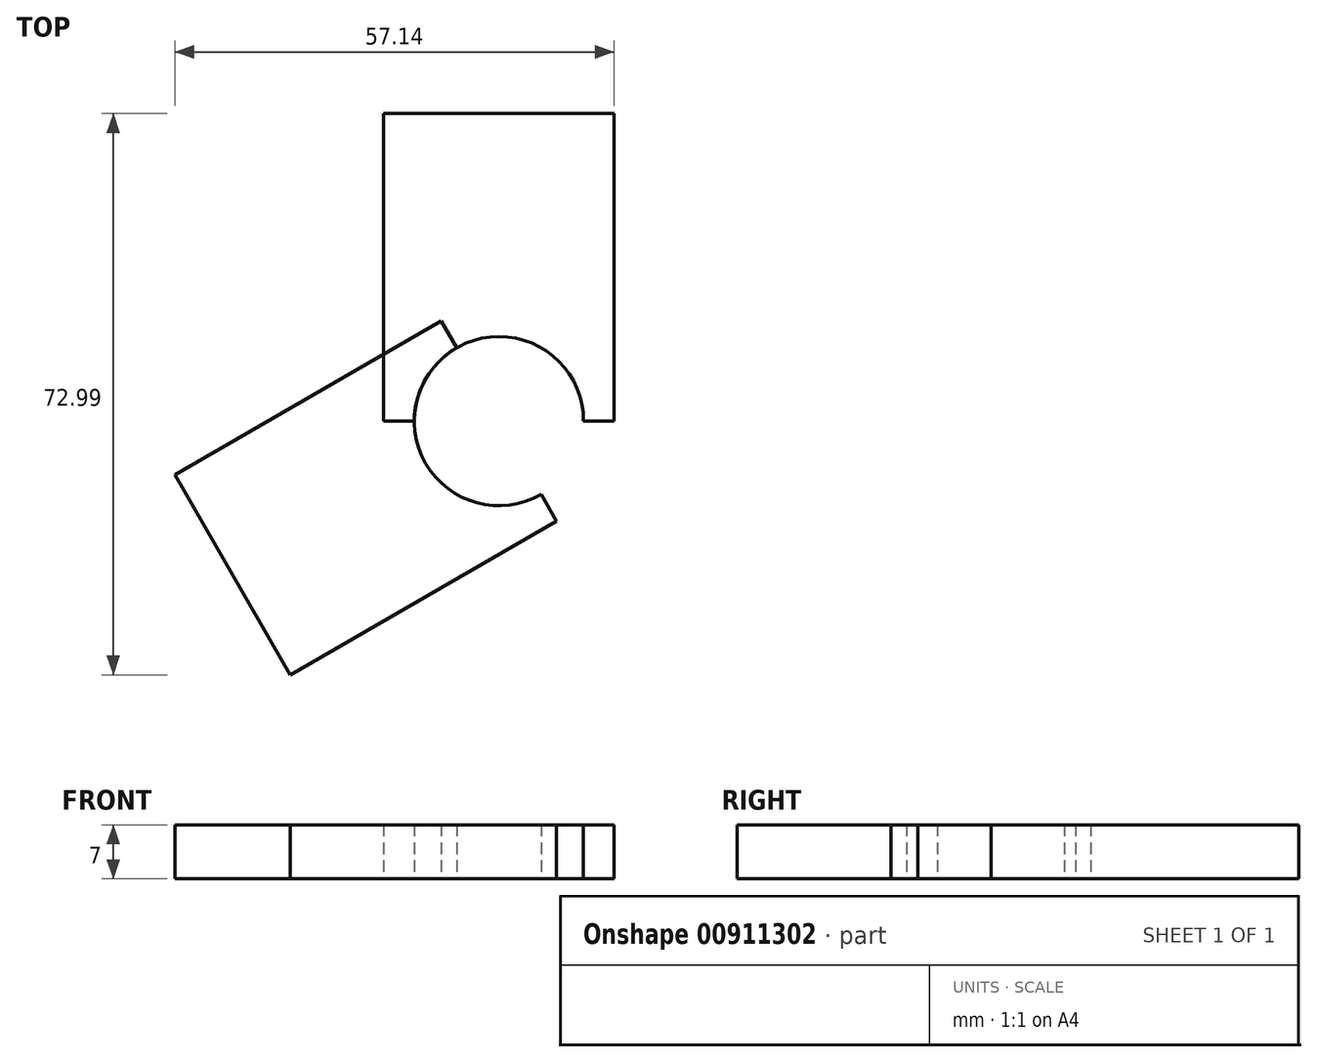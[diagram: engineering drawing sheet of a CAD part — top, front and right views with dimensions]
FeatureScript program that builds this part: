
annotation { "Feature Type Name" : "Feature", "Feature Type Description" : "" }
export const myFeature = defineFeature(function(context is Context, id is Id, definition is map)
    precondition{}
    {
        {
            var Q0;
            Q0=qCreatedBy(makeId("Top.planeOp"),FACE);
            var sketch = newSketch(context, id + "F0", { "sketchPlane" : qUnion([Q0])});
            skCircle(sketch, "E0", {"center": v(0, 0) * mm, "radius": 11 * mm});
            skLineSegment(sketch, "E1", {"start": v(0, 0) * mm, "end": v(0, 40) * mm});
            skLineSegment(sketch, "E2", {"start": v(0, 40) * mm, "end": v(15, 40) * mm});
            skLineSegment(sketch, "E3", {"start": v(15, 40) * mm, "end": v(15, 0) * mm});
            skLineSegment(sketch, "E4", {"start": v(15, 0) * mm, "end": v(0, 0) * mm});
            skLineSegment(sketch, "E5", {"start": v(0, 0) * mm, "end": v(-15, 0) * mm});
            skLineSegment(sketch, "E6", {"start": v(-15, 0) * mm, "end": v(-15, 40) * mm});
            skLineSegment(sketch, "E7", {"start": v(-15, 40) * mm, "end": v(0, 40) * mm});
            skSolve(sketch);
        }
        {
            var Q0;
            {var subQ0=sQuery(id+"F0.wireOp",EDGE,"E6");Q0=makeQuery(id+"F0.imprint","IMPRINT",FACE,{"disambiguationData":[TD([[makeQuery(id+"F0.imprint","IMPRINT",EDGE,{"derivedFrom":subQ0}),-1.0]])]});}
            var Q1;
            {var subQ1=sQuery(id+"F0.wireOp",EDGE,"E2");Q1=makeQuery(id+"F0.imprint","IMPRINT",FACE,{"disambiguationData":[TD([[makeQuery(id+"F0.imprint","IMPRINT",EDGE,{"derivedFrom":subQ1}),-1.0]])]});}
            extrude(context, id + "F1", {"entities" : qUnion([Q0, Q1]), "depth" : 7 * mm, "offsetDistance" : 25 * mm});
        }
        {
            var Q0;
            Q0=qCreatedBy(makeId("Front.planeOp"),FACE);
            var sketch = newSketch(context, id + "F2", { "sketchPlane" : qUnion([Q0])});
            skLineSegment(sketch, "E8", {"start": v(0, 0) * mm, "end": v(0, 42.87) * mm});
            skSolve(sketch);
        }
        {
            var Q0;
            Q0=makeQuery(id+"F1.opExtrude","SWEPT_BODY",BODY,{"disambiguationData":[OSD([sQuery(id+"F0.wireOp",EDGE,"E0"),sQuery(id+"F0.wireOp",EDGE,"E2"),sQuery(id+"F0.wireOp",EDGE,"E3"),sQuery(id+"F0.wireOp",EDGE,"E4"),sQuery(id+"F0.wireOp",EDGE,"E5"),sQuery(id+"F0.wireOp",EDGE,"E6"),sQuery(id+"F0.wireOp",EDGE,"E7")])]});
            var Q1;
            Q1=sQuery(id+"F2.wireOp",EDGE,"E8");
            transform(context, id + "F3", {"entities" : qUnion([Q0]), "transformType" : TransformType.ROTATION, "transformAxis" : qUnion([Q1]), "angle" : 120 * degree, "makeCopy" : true});
        }
    });
